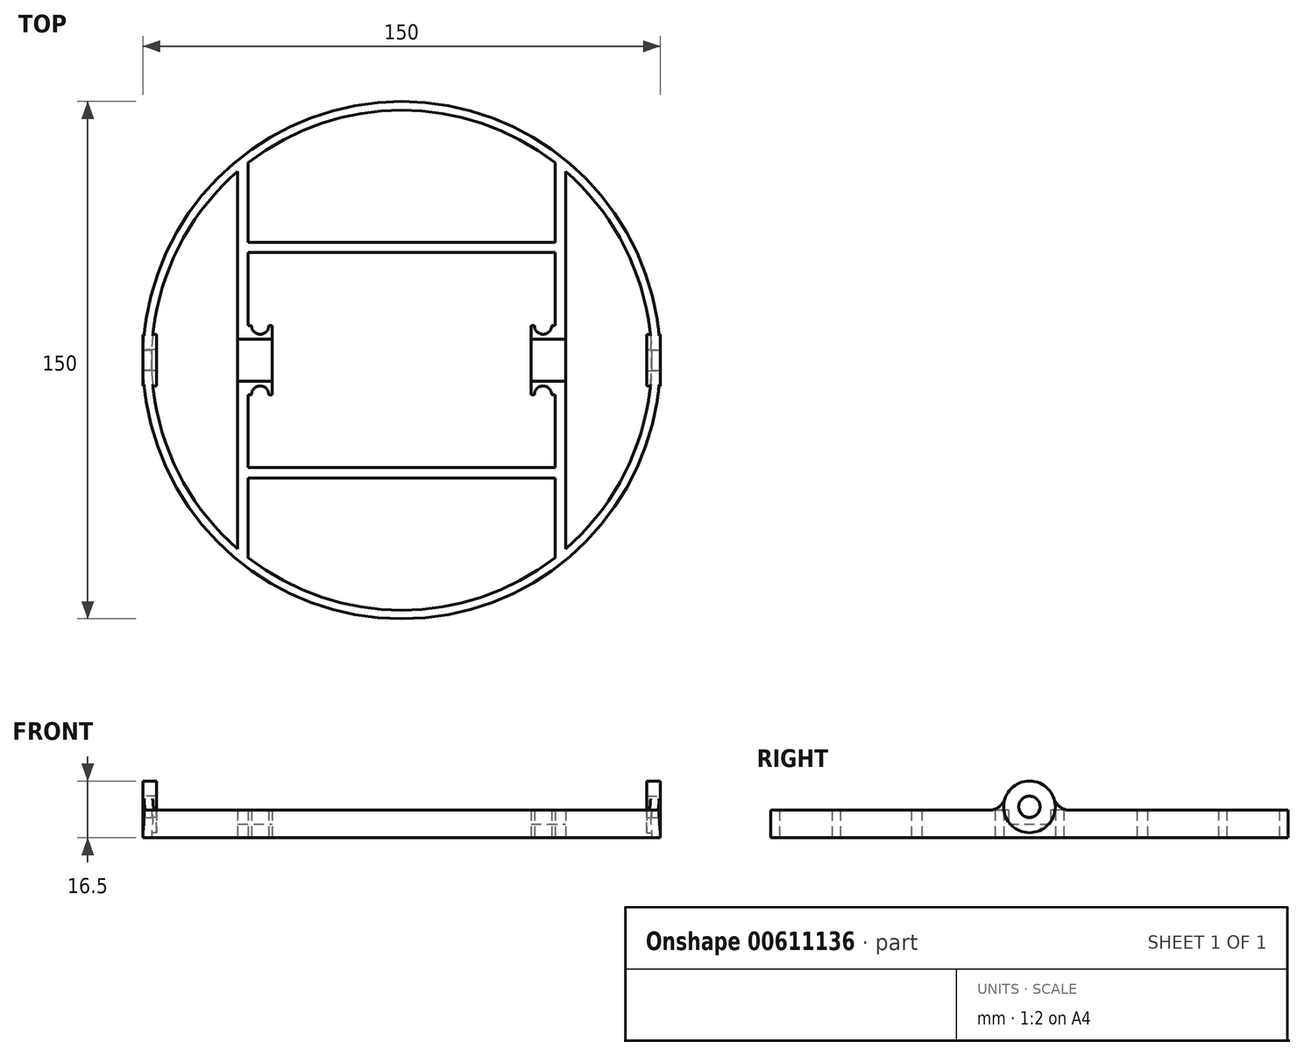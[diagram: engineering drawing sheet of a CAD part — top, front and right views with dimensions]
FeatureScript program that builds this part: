
annotation { "Feature Type Name" : "Feature", "Feature Type Description" : "" }
export const myFeature = defineFeature(function(context is Context, id is Id, definition is map)
    precondition{}
    {
        {
            var Q0;
            Q0=qCreatedBy(makeId("Top.planeOp"),FACE);
            var sketch = newSketch(context, id + "F0", { "sketchPlane" : qUnion([Q0])});
            skCircle(sketch, "E0", {"center": v(0, 0) * mm, "radius": 75 * mm});
            skCircle(sketch, "E1", {"center": v(0, 0) * mm, "radius": 72.5 * mm});
            skSolve(sketch);
        }
        {
            var Q0;
            Q0 = qSketchRegion(id + "F0", true);
            extrude(context, id + "F1", {"entities" : qUnion([Q0]), "endBound" : BoundingType.SYMMETRIC, "depth" : 8 * mm, "offsetDistance" : 25 * mm});
        }
        {
            var Q0;
            Q0=qCreatedBy(makeId("Top.planeOp"),FACE);
            var sketch = newSketch(context, id + "F2", { "sketchPlane" : qUnion([Q0])});
            skCircle(sketch, "E2.0", {"center": v(0, 0) * mm, "radius": 72.5 * mm});
            skLineSegment(sketch, "E3", {"start": v(0, 0) * mm, "end": v(-88.65, 0) * mm, "construction": true});
            skLineSegment(sketch, "E4", {"start": v(0, 0) * mm, "end": v(82.5, 0) * mm, "construction": true});
            skLineSegment(sketch, "E5", {"start": v(0, 0) * mm, "end": v(0, 78.86) * mm, "construction": true});
            skLineSegment(sketch, "E6", {"start": v(0, 0) * mm, "end": v(0, -78.18) * mm, "construction": true});
            skLineSegment(sketch, "E7", {"start": v(0, -78.18) * mm, "end": v(1.48, -78.18) * mm, "construction": true});
            skSolve(sketch);
        }
        {
            var Q0;
            Q0=qCreatedBy(makeId("Right.planeOp"),FACE);
            cPlane(context, id + "F3", {"entities" : qUnion([Q0]), "cplaneType" : CPlaneType.OFFSET, "offset" : 75 * mm, "width" : 150 * mm, "height" : 150 * mm});
        }
        {
            var Q0;
            Q0=qCreatedBy(makeId("Top.planeOp"),FACE);
            var sketch = newSketch(context, id + "F4", { "sketchPlane" : qUnion([Q0])});
            skLineSegment(sketch, "E8.bottom", {"start": v(-47.5, 57.24) * mm, "end": v(-44.5, 57.24) * mm});
            skLineSegment(sketch, "E8.top", {"start": v(-47.5, -57.24) * mm, "end": v(-44.5, -57.24) * mm});
            skLineSegment(sketch, "E8.left", {"start": v(-47.5, 57.24) * mm, "end": v(-47.5, -57.24) * mm});
            skLineSegment(sketch, "E8.right", {"start": v(-44.5, 57.24) * mm, "end": v(-44.5, -57.24) * mm});
            skLineSegment(sketch, "E9.MirrorCS", {"start": v(44.5, 57.24) * mm, "end": v(44.5, -57.24) * mm});
            skLineSegment(sketch, "E10.MirrorCS", {"start": v(47.5, 57.24) * mm, "end": v(44.5, 57.24) * mm});
            skLineSegment(sketch, "E11.MirrorCS", {"start": v(47.5, 57.24) * mm, "end": v(47.5, -57.24) * mm});
            skLineSegment(sketch, "E12.MirrorCS", {"start": v(47.5, -57.24) * mm, "end": v(44.5, -57.24) * mm});
            skLineSegment(sketch, "E13.bottom", {"start": v(-44.5, 10) * mm, "end": v(-43.5, 10) * mm});
            skLineSegment(sketch, "E13.top", {"start": v(-44.5, -10) * mm, "end": v(-43.5, -10) * mm});
            skLineSegment(sketch, "E13.left", {"start": v(-44.5, 10) * mm, "end": v(-44.5, -10) * mm});
            skLineSegment(sketch, "E13.right", {"start": v(-37.5, 10) * mm, "end": v(-37.5, -10) * mm});
            skArc(sketch, "E14", {"start": v(-43.5, 10) * mm, "mid": v(-41, 7.5) * mm, "end": v(-38.5, 10) * mm});
            skLineSegment(sketch, "E15.trimOffspring", {"start": v(-38.5, 10) * mm, "end": v(-37.5, 10) * mm});
            skArc(sketch, "E16", {"start": v(-38.5, -10) * mm, "mid": v(-41, -7.5) * mm, "end": v(-43.5, -10) * mm});
            skLineSegment(sketch, "E17.trimOffspring", {"start": v(-38.5, -10) * mm, "end": v(-37.5, -10) * mm});
            skLineSegment(sketch, "E18.bottom", {"start": v(-44.5, 34.18) * mm, "end": v(44.5, 34.18) * mm});
            skLineSegment(sketch, "E18.top", {"start": v(-44.5, 31.18) * mm, "end": v(44.5, 31.18) * mm});
            skLineSegment(sketch, "E18.left", {"start": v(-44.5, 34.18) * mm, "end": v(-44.5, 31.18) * mm});
            skLineSegment(sketch, "E18.right", {"start": v(44.5, 34.18) * mm, "end": v(44.5, 31.18) * mm});
            skLineSegment(sketch, "E19.MirrorCS", {"start": v(-44.5, -34.18) * mm, "end": v(44.5, -34.18) * mm});
            skLineSegment(sketch, "E20.MirrorCS", {"start": v(-44.5, -31.18) * mm, "end": v(44.5, -31.18) * mm});
            skSolve(sketch);
        }
        {
            var Q0;
            Q0 = qSketchRegion(id + "F4", true);
            var Q1;
            Q1=makeQuery(id+"F4.imprint","IMPRINT",FACE,{"disambiguationData":[TD([[makeQuery(id+"F4.imprint","IMPRINT",EDGE,{"derivedFrom":sQuery(id+"F4.wireOp",EDGE,"E13.bottom")}),-1.0]])]});
            extrude(context, id + "F5", {"entities" : qUnion([Q0, Q1]), "operationType" : NewBodyOperationType.ADD, "endBound" : BoundingType.SYMMETRIC, "depth" : 8 * mm, "offsetDistance" : 25 * mm});
        }
        {
            var Q0;
            Q0=makeQuery(id+"F1.opExtrude","CAP_FACE",FACE,{"disambiguationData":[OSD([sQuery(id+"F0.wireOp",EDGE,"E0"),sQuery(id+"F0.wireOp",EDGE,"E1")])],"isStart":false});
            var sketch = newSketch(context, id + "F6", { "sketchPlane" : qUnion([Q0])});
            skPoint(sketch, "E21", {"position": v(-75, 0) * mm});
            skSolve(sketch);
        }
        {
            var Q0;
            Q0=qCreatedBy(makeId("Right.planeOp"),FACE);
            var sketch = newSketch(context, id + "F7", { "sketchPlane" : qUnion([Q0])});
            skCircle(sketch, "E22", {"center": v(0, 5) * mm, "radius": 3.05 * mm});
            skLineSegment(sketch, "E23.bottom", {"start": v(-6.1, 10) * mm, "end": v(6.1, 10) * mm});
            skLineSegment(sketch, "E23.top", {"start": v(-6.1, 0) * mm, "end": v(6.1, 0) * mm});
            skLineSegment(sketch, "E23.left", {"start": v(-6.1, 10) * mm, "end": v(-6.1, 0) * mm});
            skLineSegment(sketch, "E23.right", {"start": v(6.1, 10) * mm, "end": v(6.1, 0) * mm});
            skSolve(sketch);
        }
        {
            var Q0;
            Q0=makeQuery(id+"F7.imprint","IMPRINT",FACE,{"disambiguationData":[TD([[makeQuery(id+"F7.imprint","IMPRINT",EDGE,{"derivedFrom":sQuery(id+"F7.wireOp",EDGE,"E22")}),1.0]])]});
            var Q1;
            Q1=sQuery(id+"F7.wireOp",EDGE,"E22");
            extrude(context, id + "F8", {"entities" : qUnion([Q0]), "operationType" : NewBodyOperationType.REMOVE, "surfaceEntities" : qUnion([Q1]), "endBound" : BoundingType.SYMMETRIC, "oppositeDirection" : true, "depth" : 160 * mm, "offsetDistance" : 25 * mm});
        }
        {
            var Q0;
            Q0 = qSketchRegion(id + "F7", true);
            extrude(context, id + "F9", {"entities" : qUnion([Q0]), "operationType" : NewBodyOperationType.REMOVE, "endBound" : BoundingType.SYMMETRIC, "oppositeDirection" : true, "depth" : 100 * mm, "offsetDistance" : 25 * mm});
        }
        {
            var Q0;
            Q0=qCreatedBy(makeId("Right.planeOp"),FACE);
            var Q1;
            Q1=sQuery(id+"F6.wireOp",VERTEX,"E21");
            cPlane(context, id + "F10", {"entities" : qUnion([Q0, Q1]), "cplaneType" : CPlaneType.PLANE_POINT, "offset" : 25 * mm, "width" : 150 * mm, "height" : 150 * mm});
        }
        {
            var Q0;
            Q0=qCreatedBy(id+"F10.planeOp",FACE);
            var sketch = newSketch(context, id + "F11", { "sketchPlane" : qUnion([Q0])});
            skCircle(sketch, "E24", {"center": v(0, 5) * mm, "radius": 7.5 * mm});
            skCircle(sketch, "E25", {"center": v(0, 5) * mm, "radius": 3.1 * mm});
            skLineSegment(sketch, "E26", {"start": v(3.1, 5) * mm, "end": v(7.5, 5) * mm, "construction": true});
            skLineSegment(sketch, "E27", {"start": v(7.5, 5) * mm, "end": v(3.1, 5) * mm, "construction": true});
            skLineSegment(sketch, "E28.trimOffspring", {"start": v(-3.1, 5) * mm, "end": v(-7.5, 5) * mm, "construction": true});
            skSolve(sketch);
        }
        {
            var Q0;
            Q0=makeQuery(id+"F11.imprint","IMPRINT",FACE,{"disambiguationData":[TD([[makeQuery(id+"F11.imprint","IMPRINT",EDGE,{"derivedFrom":sQuery(id+"F11.wireOp",EDGE,"E24")}),1.0]])]});
            extrude(context, id + "F12", {"entities" : qUnion([Q0]), "operationType" : NewBodyOperationType.ADD, "depth" : 4 * mm, "offsetDistance" : 25 * mm});
        }
        {
            var Q0;
            {var subQ0=sQuery(id+"F4.wireOp",EDGE,"E19.MirrorCS");var subQ1=sQuery(id+"F4.wireOp",EDGE,"E11.MirrorCS");var subQ2=sQuery(id+"F4.wireOp",EDGE,"E12.MirrorCS");var subQ3=sQuery(id+"F4.wireOp",EDGE,"E9.MirrorCS");var subQ4=sQuery(id+"F4.wireOp",EDGE,"E18.top");var subQ5=sQuery(id+"F4.wireOp",EDGE,"E20.MirrorCS");var subQ6=sQuery(id+"F4.wireOp",EDGE,"E8.right");var subQ7=sQuery(id+"F4.wireOp",EDGE,"E8.top");var subQ8=sQuery(id+"F0.wireOp",EDGE,"E0");var subQ9=sQuery(id+"F4.wireOp",EDGE,"E13.left");var subQ10=sQuery(id+"F0.wireOp",EDGE,"E1");var subQ11=sQuery(id+"F4.wireOp",EDGE,"E8.left");Q0=makeQuery(id+"F12.boolean.opBoolean","INTERSECT",EDGE,{"derivedFrom":[makeQuery(id+"F8.boolean.opBoolean","SPLIT",FACE,{"disambiguationData":[TD([makeQuery(id+"F5.opExtrude","SWEPT_FACE",FACE,{"disambiguationData":[OSD([subQ0])]})])],"derivedFrom":makeQuery(id+"F5.boolean.opBoolean","MERGE",FACE,{"derivedFrom":[makeQuery(id+"F1.opExtrude","CAP_FACE",FACE,{"disambiguationData":[OSD([subQ8,subQ10])],"isStart":false}),makeQuery(id+"F5.opExtrude","CAP_FACE",FACE,{"disambiguationData":[OSD([sQuery(id+"F4.wireOp",EDGE,"E8.bottom"),subQ7,subQ11,subQ6,subQ3,sQuery(id+"F4.wireOp",EDGE,"E10.MirrorCS"),subQ1,subQ2,subQ9,sQuery(id+"F4.wireOp",EDGE,"E18.bottom"),subQ4,subQ0,subQ5])],"isStart":false})]})}),makeQuery(id+"F12.opExtrude","SWEPT_FACE",FACE,{"disambiguationData":[OSD([sQuery(id+"F11.wireOp",EDGE,"E24")])]})]});}
            var Q1;
            {var subQ0=sQuery(id+"F4.wireOp",EDGE,"E18.bottom");var subQ1=sQuery(id+"F0.wireOp",EDGE,"E1");var subQ2=sQuery(id+"F4.wireOp",EDGE,"E11.MirrorCS");var subQ4=sQuery(id+"F4.wireOp",EDGE,"E18.top");var subQ5=sQuery(id+"F4.wireOp",EDGE,"E9.MirrorCS");var subQ6=sQuery(id+"F4.wireOp",EDGE,"E20.MirrorCS");var subQ7=sQuery(id+"F4.wireOp",EDGE,"E13.left");var subQ8=sQuery(id+"F4.wireOp",EDGE,"E8.right");var subQ9=sQuery(id+"F4.wireOp",EDGE,"E10.MirrorCS");var subQ10=sQuery(id+"F0.wireOp",EDGE,"E0");var subQ11=sQuery(id+"F4.wireOp",EDGE,"E8.left");var subQ12=sQuery(id+"F4.wireOp",EDGE,"E8.bottom");Q1=makeQuery(id+"F12.boolean.opBoolean","INTERSECT",EDGE,{"derivedFrom":[makeQuery(id+"F8.boolean.opBoolean","SPLIT",FACE,{"disambiguationData":[TD([makeQuery(id+"F5.opExtrude","SWEPT_FACE",FACE,{"disambiguationData":[OSD([subQ0])]})])],"derivedFrom":makeQuery(id+"F5.boolean.opBoolean","MERGE",FACE,{"derivedFrom":[makeQuery(id+"F1.opExtrude","CAP_FACE",FACE,{"disambiguationData":[OSD([subQ10,subQ1])],"isStart":false}),makeQuery(id+"F5.opExtrude","CAP_FACE",FACE,{"disambiguationData":[OSD([subQ12,sQuery(id+"F4.wireOp",EDGE,"E8.top"),subQ11,subQ8,subQ5,subQ9,subQ2,sQuery(id+"F4.wireOp",EDGE,"E12.MirrorCS"),subQ7,subQ0,subQ4,sQuery(id+"F4.wireOp",EDGE,"E19.MirrorCS"),subQ6])],"isStart":false})]})}),makeQuery(id+"F12.opExtrude","SWEPT_FACE",FACE,{"disambiguationData":[OSD([sQuery(id+"F11.wireOp",EDGE,"E24")])]})]});}
            fillet(context, id + "F13", {"entities" : qUnion([Q0, Q1]), "radius" : 5 * mm, "tangentPropagation" : true, "allowEdgeOverflow" : false});
        }
        {
            var Q0;
            Q0=makeQuery(id+"F1.opExtrude","SWEPT_BODY",BODY,{"disambiguationData":[OSD([sQuery(id+"F0.wireOp",EDGE,"E0"),sQuery(id+"F0.wireOp",EDGE,"E1")])]});
            var Q1;
            Q1=qCreatedBy(makeId("Right.planeOp"),FACE);
            mirror(context, id + "F14", {"operationType" : NewBodyOperationType.ADD, "entities" : qUnion([Q0]), "mirrorPlane" : qUnion([Q1])});
        }
    });
